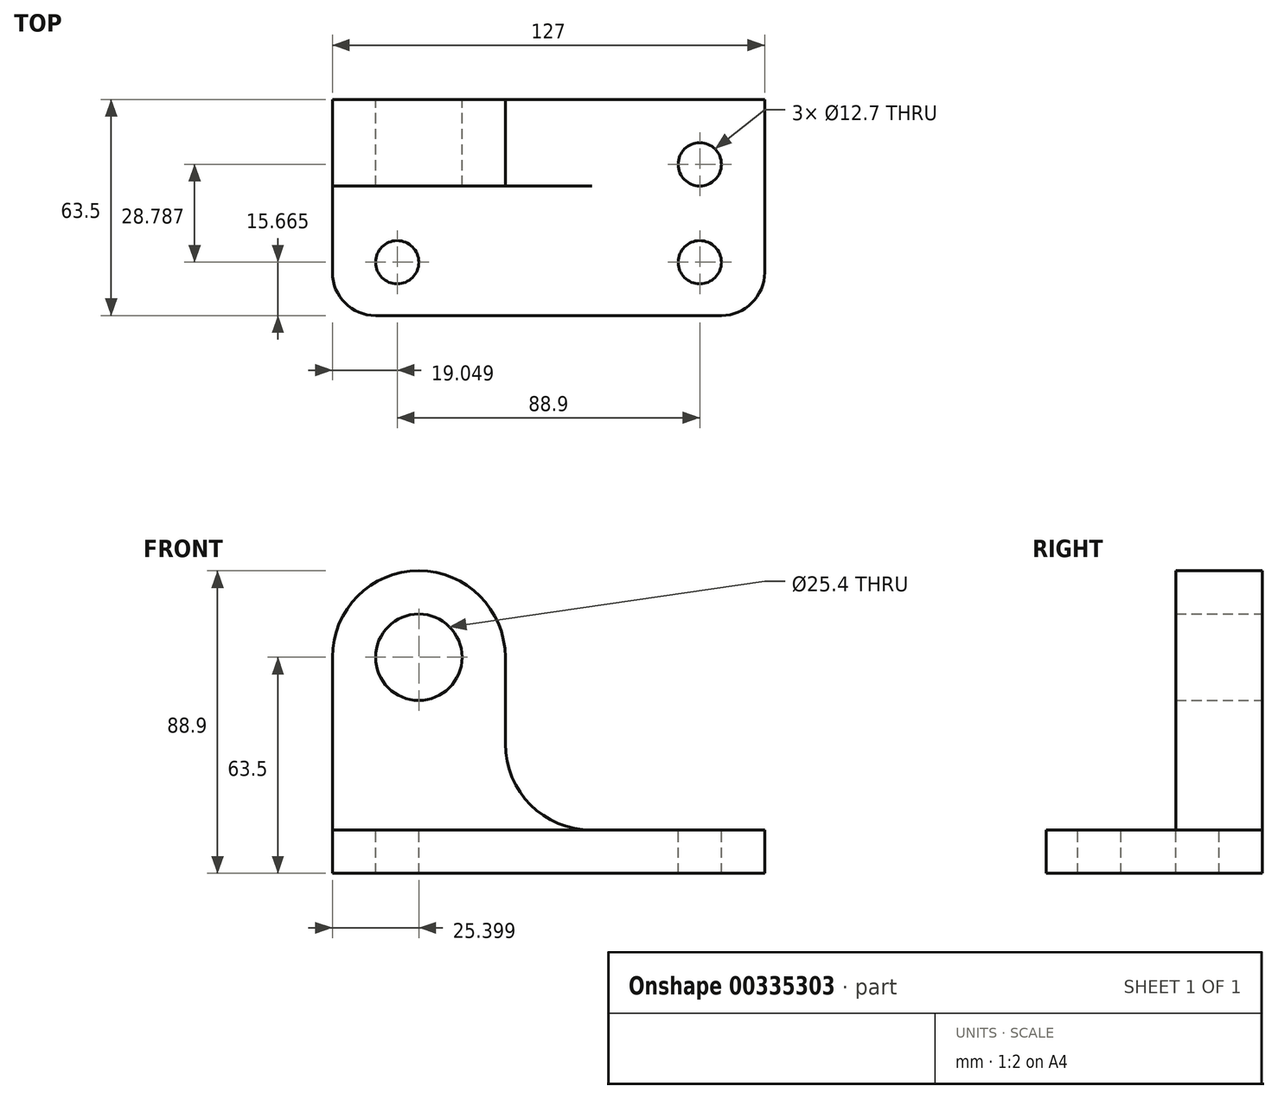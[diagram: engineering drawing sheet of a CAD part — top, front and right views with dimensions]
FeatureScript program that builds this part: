
annotation { "Feature Type Name" : "Feature", "Feature Type Description" : "" }
export const myFeature = defineFeature(function(context is Context, id is Id, definition is map)
    precondition{}
    {
        {
            var Q0;
            Q0=qCreatedBy(makeId("Top.planeOp"),FACE);
            var sketch = newSketch(context, id + "F0", { "sketchPlane" : qUnion([Q0])});
            skLineSegment(sketch, "E0.bottom", {"start": v(-44, -41.2) * mm, "end": v(57.6, -41.2) * mm});
            skLineSegment(sketch, "E0.top", {"start": v(-56.7, 22.3) * mm, "end": v(70.3, 22.3) * mm});
            skLineSegment(sketch, "E0.left", {"start": v(-56.7, -28.5) * mm, "end": v(-56.7, 22.3) * mm});
            skLineSegment(sketch, "E0.right", {"start": v(70.3, -28.5) * mm, "end": v(70.3, 22.3) * mm});
            skPoint(sketch, "E1.visualSharp", {"position": v(-56.7, -41.2) * mm});
            skArc(sketch, "E1.filletArc", {"start": v(-56.7, -28.5) * mm, "mid": v(-52.97, -37.48) * mm, "end": v(-44, -41.2) * mm});
            skPoint(sketch, "E2.visualSharp", {"position": v(70.3, -41.2) * mm});
            skArc(sketch, "E2.filletArc", {"start": v(57.6, -41.2) * mm, "mid": v(66.59, -37.48) * mm, "end": v(70.3, -28.5) * mm});
            skSolve(sketch);
        }
        {
            var Q0;
            Q0=makeQuery(id+"F0.imprint","IMPRINT",FACE,{"disambiguationData":[TD([[makeQuery(id+"F0.imprint","IMPRINT",EDGE,{"derivedFrom":sQuery(id+"F0.wireOp",EDGE,"E0.bottom")}),1.0]])]});
            extrude(context, id + "F1", {"entities" : qUnion([Q0]), "depth" : 12.7 * mm});
        }
        {
            var Q0;
            Q0=makeQuery(id+"F1.opExtrude","CAP_FACE",FACE,{"disambiguationData":[OSD([sQuery(id+"F0.wireOp",EDGE,"E0.bottom"),sQuery(id+"F0.wireOp",EDGE,"E0.top"),sQuery(id+"F0.wireOp",EDGE,"E0.left"),sQuery(id+"F0.wireOp",EDGE,"E0.right"),sQuery(id+"F0.wireOp",EDGE,"E1.filletArc"),sQuery(id+"F0.wireOp",EDGE,"E2.filletArc")])],"isStart":false});
            var sketch = newSketch(context, id + "F2", { "sketchPlane" : qUnion([Q0])});
            skLineSegment(sketch, "E3", {"start": v(70.3, 22.3) * mm, "end": v(51.26, 22.3) * mm});
            skLineSegment(sketch, "E4", {"start": v(70.3, 22.3) * mm, "end": v(70.3, 3.25) * mm});
            skCircle(sketch, "E5", {"center": v(51.26, 3.25) * mm, "radius": 6.35 * mm});
            skCircle(sketch, "E6", {"center": v(51.26, -25.54) * mm, "radius": 6.35 * mm});
            skLineSegment(sketch, "E7", {"start": v(-56.7, -41.2) * mm, "end": v(-37.64, -41.2) * mm});
            skCircle(sketch, "E8", {"center": v(-37.64, -25.54) * mm, "radius": 6.35 * mm});
            skSolve(sketch);
        }
        {
            var Q0;
            Q0=makeQuery(id+"F2.imprint","IMPRINT",FACE,{"disambiguationData":[TD([[makeQuery(id+"F2.imprint","IMPRINT",EDGE,{"derivedFrom":sQuery(id+"F2.wireOp",EDGE,"E8")}),1.0]])]});
            var Q1;
            Q1=makeQuery(id+"F2.imprint","IMPRINT",FACE,{"disambiguationData":[TD([[makeQuery(id+"F2.imprint","IMPRINT",EDGE,{"derivedFrom":sQuery(id+"F2.wireOp",EDGE,"E6")}),1.0]])]});
            var Q2;
            Q2=makeQuery(id+"F2.imprint","IMPRINT",FACE,{"disambiguationData":[TD([[makeQuery(id+"F2.imprint","IMPRINT",EDGE,{"derivedFrom":sQuery(id+"F2.wireOp",EDGE,"E5")}),1.0]])]});
            extrude(context, id + "F3", {"entities" : qUnion([Q0, Q1, Q2]), "operationType" : NewBodyOperationType.REMOVE, "oppositeDirection" : true, "depth" : 12.7 * mm});
        }
        {
            var Q0;
            Q0=makeQuery(id+"F1.opExtrude","SWEPT_FACE",FACE,{"disambiguationData":[OSD([sQuery(id+"F0.wireOp",EDGE,"E0.top")])]});
            var sketch = newSketch(context, id + "F4", { "sketchPlane" : qUnion([Q0])});
            skLineSegment(sketch, "E9", {"start": v(5.9, 38.1) * mm, "end": v(5.9, 63.5) * mm});
            skLineSegment(sketch, "E10", {"start": v(56.7, 63.5) * mm, "end": v(56.7, 12.7) * mm});
            skArc(sketch, "E11", {"start": v(56.7, 63.5) * mm, "mid": v(31.3, 88.9) * mm, "end": v(5.9, 63.5) * mm});
            skCircle(sketch, "E12", {"center": v(31.3, 63.5) * mm, "radius": 12.7 * mm});
            skArc(sketch, "E13", {"start": v(-19.5, 12.7) * mm, "mid": v(-1.55, 20.14) * mm, "end": v(5.9, 38.1) * mm});
            skLineSegment(sketch, "E14", {"start": v(56.7, 12.7) * mm, "end": v(-19.5, 12.7) * mm});
            skSolve(sketch);
        }
        {
            var Q0;
            Q0=makeQuery(id+"F4.imprint","IMPRINT",FACE,{"disambiguationData":[TD([[makeQuery(id+"F4.imprint","IMPRINT",EDGE,{"derivedFrom":sQuery(id+"F4.wireOp",EDGE,"E9")}),-1.0]])]});
            extrude(context, id + "F5", {"entities" : qUnion([Q0]), "operationType" : NewBodyOperationType.ADD, "oppositeDirection" : true, "depth" : 25.4 * mm});
        }
    });
